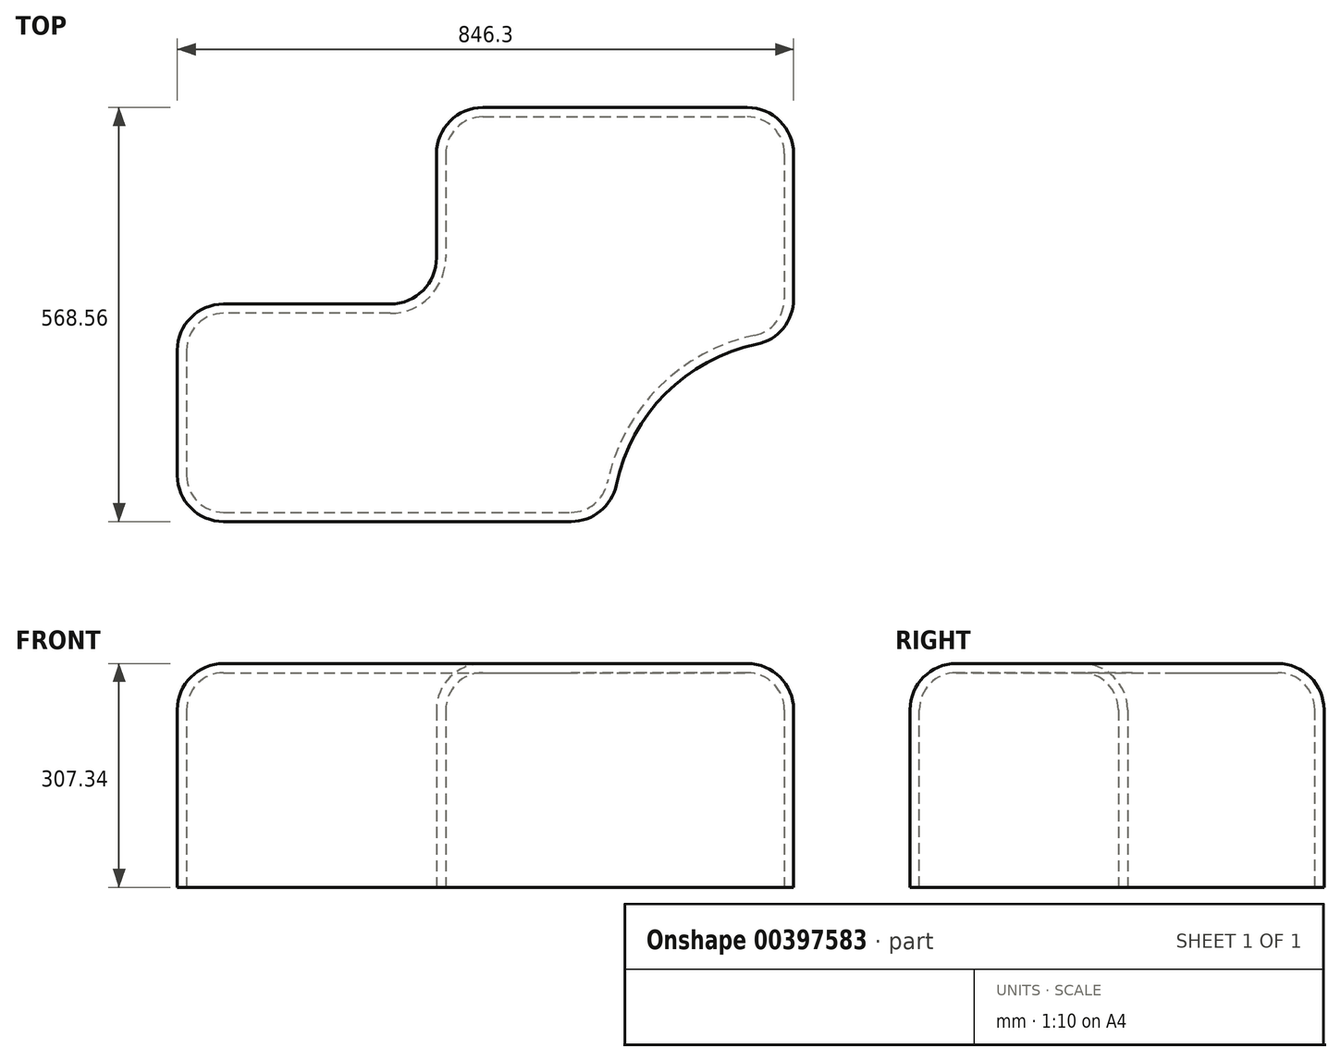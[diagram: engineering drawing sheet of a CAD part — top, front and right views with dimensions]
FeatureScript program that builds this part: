
annotation { "Feature Type Name" : "Feature", "Feature Type Description" : "" }
export const myFeature = defineFeature(function(context is Context, id is Id, definition is map)
    precondition{}
    {
        {
            var Q0;
            Q0=qCreatedBy(makeId("Top.planeOp"),FACE);
            var sketch = newSketch(context, id + "F0", { "sketchPlane" : qUnion([Q0])});
            skLineSegment(sketch, "E0.bottom", {"start": v(158.85, 191.5) * mm, "end": v(649.23, 191.5) * mm});
            skLineSegment(sketch, "E0.top", {"start": v(-197.07, -377.06) * mm, "end": v(400.64, -377.06) * mm});
            skLineSegment(sketch, "E0.left", {"start": v(-197.07, -78.35) * mm, "end": v(-197.07, -377.06) * mm});
            skLineSegment(sketch, "E0.right", {"start": v(649.23, 191.5) * mm, "end": v(649.23, -128.47) * mm});
            skLineSegment(sketch, "E1", {"start": v(158.85, 191.5) * mm, "end": v(158.85, -78.35) * mm});
            skLineSegment(sketch, "E2", {"start": v(158.85, -78.35) * mm, "end": v(-197.07, -78.35) * mm});
            skArc(sketch, "E3", {"start": v(649.23, -128.47) * mm, "mid": v(473.45, -201.28) * mm, "end": v(400.64, -377.06) * mm});
            skSolve(sketch);
        }
        {
            var Q0;
            Q0=makeQuery(id+"F0.imprint","IMPRINT",FACE,{"disambiguationData":[TD([[makeQuery(id+"F0.imprint","IMPRINT",EDGE,{"derivedFrom":sQuery(id+"F0.wireOp",EDGE,"E0.bottom")}),-1.0]])]});
            extrude(context, id + "F1", {"entities" : qUnion([Q0]), "depth" : 307.34 * mm});
        }
        {
            var Q0;
            Q0=makeQuery(id+"F1.opExtrude","SWEPT_EDGE",EDGE,{"disambiguationData":[OSD([sQuery(id+"F0.wireOp",EDGE,"E0.bottom"),sQuery(id+"F0.wireOp",EDGE,"E1")])]});
            var Q1;
            Q1=makeQuery(id+"F1.opExtrude","SWEPT_EDGE",EDGE,{"disambiguationData":[OSD([sQuery(id+"F0.wireOp",EDGE,"E1"),sQuery(id+"F0.wireOp",EDGE,"E2")])]});
            var Q2;
            Q2=makeQuery(id+"F1.opExtrude","SWEPT_EDGE",EDGE,{"disambiguationData":[OSD([sQuery(id+"F0.wireOp",EDGE,"E0.left"),sQuery(id+"F0.wireOp",EDGE,"E2")])]});
            var Q3;
            Q3=makeQuery(id+"F1.opExtrude","SWEPT_EDGE",EDGE,{"disambiguationData":[OSD([sQuery(id+"F0.wireOp",EDGE,"E0.top"),sQuery(id+"F0.wireOp",EDGE,"E0.left")])]});
            var Q4;
            Q4=makeQuery(id+"F1.opExtrude","SWEPT_EDGE",EDGE,{"disambiguationData":[OSD([sQuery(id+"F0.wireOp",EDGE,"E0.right"),sQuery(id+"F0.wireOp",EDGE,"E3")])]});
            var Q5;
            Q5=makeQuery(id+"F1.opExtrude","SWEPT_EDGE",EDGE,{"disambiguationData":[OSD([sQuery(id+"F0.wireOp",EDGE,"E0.top"),sQuery(id+"F0.wireOp",EDGE,"E3")])]});
            var Q6;
            Q6=makeQuery(id+"F1.opExtrude","SWEPT_EDGE",EDGE,{"disambiguationData":[OSD([sQuery(id+"F0.wireOp",EDGE,"E0.bottom"),sQuery(id+"F0.wireOp",EDGE,"E0.right")])]});
            fillet(context, id + "F2", {"entities" : qUnion([Q0, Q1, Q2, Q3, Q4, Q5, Q6]), "radius" : 63.5 * mm, "tangentPropagation" : true, "allowEdgeOverflow" : false});
        }
        {
            var Q0;
            Q0=makeQuery(id+"F1.opExtrude","CAP_FACE",FACE,{"disambiguationData":[OSD([sQuery(id+"F0.wireOp",EDGE,"E0.bottom"),sQuery(id+"F0.wireOp",EDGE,"E0.top"),sQuery(id+"F0.wireOp",EDGE,"E0.left"),sQuery(id+"F0.wireOp",EDGE,"E0.right"),sQuery(id+"F0.wireOp",EDGE,"E1"),sQuery(id+"F0.wireOp",EDGE,"E2"),sQuery(id+"F0.wireOp",EDGE,"E3")])],"isStart":false});
            fillet(context, id + "F3", {"entities" : qUnion([Q0]), "radius" : 63.5 * mm, "tangentPropagation" : true, "allowEdgeOverflow" : false});
        }
        {
            var Q0;
            Q0=makeQuery(id+"F1.opExtrude","CAP_FACE",FACE,{"disambiguationData":[OSD([sQuery(id+"F0.wireOp",EDGE,"E0.bottom"),sQuery(id+"F0.wireOp",EDGE,"E0.top"),sQuery(id+"F0.wireOp",EDGE,"E0.left"),sQuery(id+"F0.wireOp",EDGE,"E0.right"),sQuery(id+"F0.wireOp",EDGE,"E1"),sQuery(id+"F0.wireOp",EDGE,"E2"),sQuery(id+"F0.wireOp",EDGE,"E3")])],"isStart":true});
            shell(context, id + "F4", {"entities" : qUnion([Q0]), "thickness" : 12.7 * mm});
        }
    });
